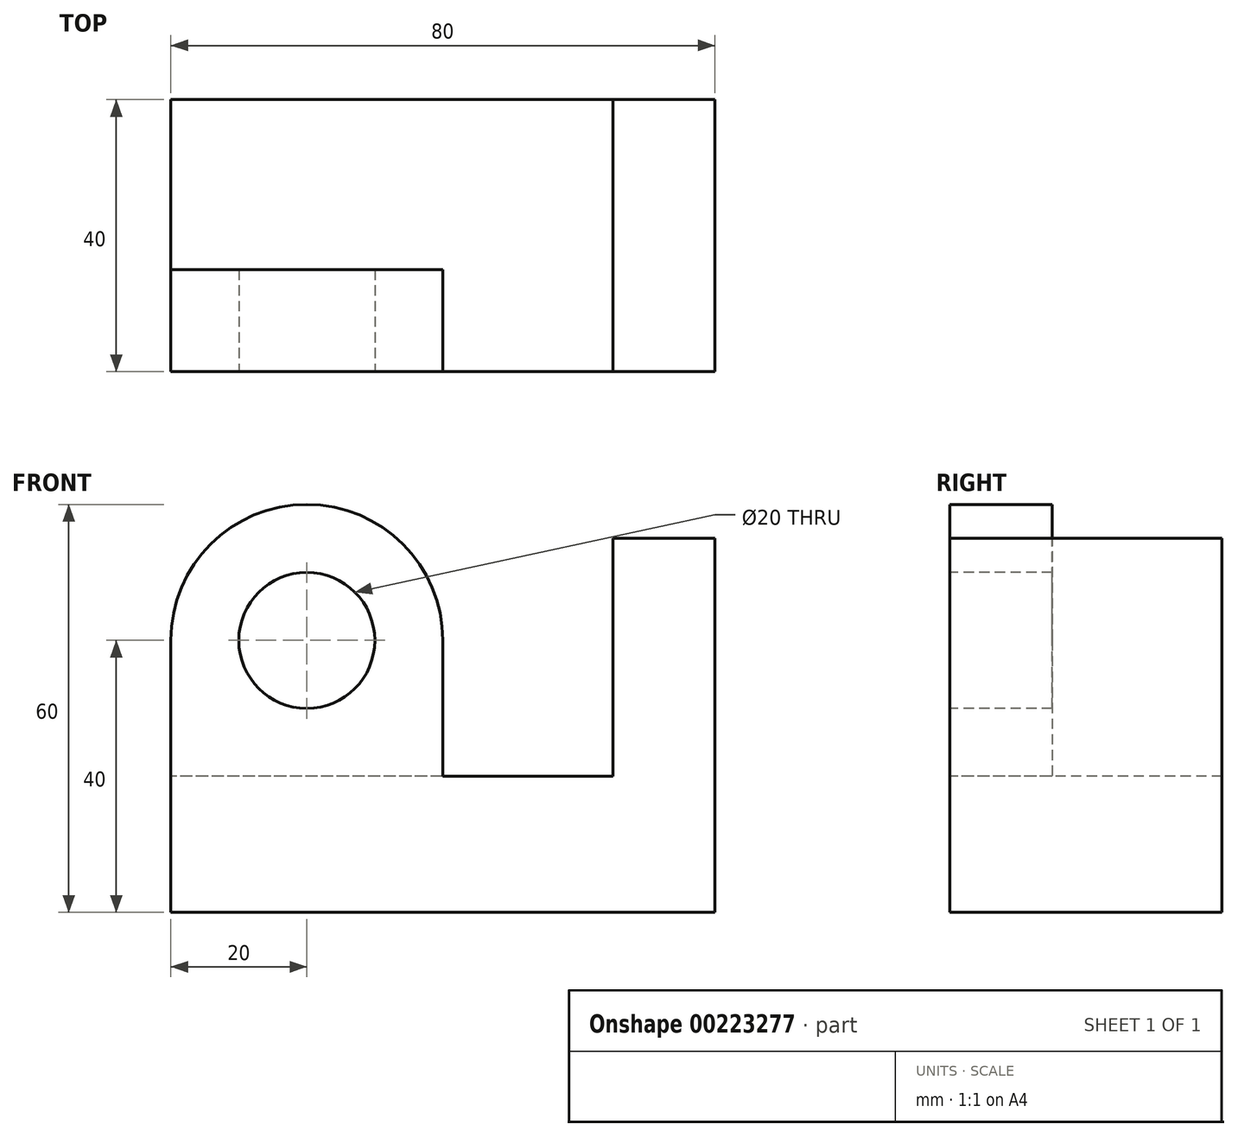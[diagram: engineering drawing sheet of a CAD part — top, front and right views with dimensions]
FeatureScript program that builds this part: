
annotation { "Feature Type Name" : "Feature", "Feature Type Description" : "" }
export const myFeature = defineFeature(function(context is Context, id is Id, definition is map)
    precondition{}
    {
        {
            var Q0;
            Q0=qCreatedBy(makeId("Front.planeOp"),FACE);
            var sketch = newSketch(context, id + "F0", { "sketchPlane" : qUnion([Q0])});
            skLineSegment(sketch, "E0", {"start": v(0, 0) * mm, "end": v(80, 0) * mm});
            skLineSegment(sketch, "E1", {"start": v(80, 0) * mm, "end": v(80, 55) * mm});
            skLineSegment(sketch, "E2", {"start": v(80, 55) * mm, "end": v(65, 55) * mm});
            skLineSegment(sketch, "E3", {"start": v(65, 55) * mm, "end": v(65, 20) * mm});
            skLineSegment(sketch, "E4", {"start": v(65, 20) * mm, "end": v(0, 20) * mm});
            skLineSegment(sketch, "E5", {"start": v(0, 20) * mm, "end": v(0, 0) * mm});
            skArc(sketch, "E6", {"start": v(40, 40) * mm, "mid": v(20, 60) * mm, "end": v(0, 40) * mm});
            skCircle(sketch, "E7", {"center": v(20, 40) * mm, "radius": 10 * mm});
            skLineSegment(sketch, "E8", {"start": v(0, 40) * mm, "end": v(0, 20) * mm});
            skLineSegment(sketch, "E9", {"start": v(40, 40) * mm, "end": v(40, 20) * mm});
            skSolve(sketch);
        }
        {
            var Q0;
            Q0=makeQuery(id+"F0.imprint","IMPRINT",FACE,{"disambiguationData":[TD([[makeQuery(id+"F0.imprint","IMPRINT",EDGE,{"derivedFrom":sQuery(id+"F0.wireOp",EDGE,"E0")}),1.0]])]});
            extrude(context, id + "F1", {"entities" : qUnion([Q0]), "oppositeDirection" : true, "depth" : 40 * mm});
        }
        {
            var Q0;
            Q0=makeQuery(id+"F0.imprint","IMPRINT",FACE,{"disambiguationData":[TD([[makeQuery(id+"F0.imprint","IMPRINT",EDGE,{"derivedFrom":sQuery(id+"F0.wireOp",EDGE,"E6")}),1.0]])]});
            extrude(context, id + "F2", {"entities" : qUnion([Q0]), "operationType" : NewBodyOperationType.ADD, "oppositeDirection" : true, "depth" : 15 * mm});
        }
    });
